# Revit family: Showerhead-Round-Grohe-Smartactive-26789_Series
name_source: partatom
category: Plumbing Fixtures
units: mm (PartAtom-declared; Revit-internal decimal feet)

## family parameters
Always vertical = No
Cut with Voids When Loaded = No
OmniClass Number = 23.45.05.14.17
OmniClass Title = Showers
Part Type = Normal
Room Calculation Point = No
Round Connector Dimension = Use Diameter
Shared = Yes
Work Plane-Based = Yes

## types (4) — shared parameters
Assembly Code = D2010710
CW Connection = No
CWFU = 3
Default Elevation = 0"
Description = RSH SMARTACTIVE 6 1/2 inch Showerhead, Round
HW Connection = No
HWFU = 3
Height = 3 1/4"
Manufacturer = Grohe
Price = Prices may vary. Please consult Manufacturer Representative for most up-to-date price list.
Tempered Water Connection = Yes
Tempered Water Connection Diameter = 1/2"
URL = https://www.grohe.us
Vent Connection = No
WFU = 4
Waste Connection = No
Width = 6 1/2"

## per-type parameters (varying)
| type | Finish | Material |
| 26789000 | Plastic-Grohe-StarLight Chrome | Plastic-Grohe-StarLight Chrome |
| 26789EN0 | Plastic-Grohe-Brushed Nickel Infinity Finish | Plastic-Grohe-Brushed Nickel Infinity Finish |
| 26789GN0 | Plastic-Grohe-Brushed Cool Sunrise | Plastic-Grohe-Brushed Cool Sunrise |
| 26789A00 | Plastic-Grohe-Hard Graphite | Plastic-Grohe-Hard Graphite |

note: column(s) folded — value = type name in every type: Model

## geometry (parser evidence)
native form markers: Sweep x2
no freeform markers — native parametric forms only
